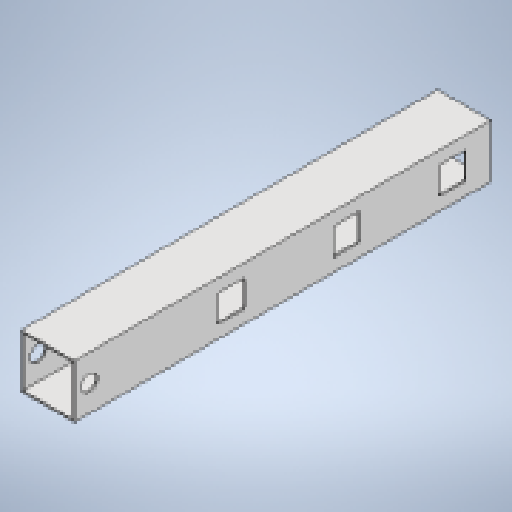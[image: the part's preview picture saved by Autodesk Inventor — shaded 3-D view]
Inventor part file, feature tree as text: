
AUTODESK INVENTOR PART (.ipt)
format: ipt  version: 2025.1 (Build 291241020, 241B)  size: 260,096 bytes
history: native  units: mm
features: sketch x4, projected_geometry x3, extrude x2, fillet x1
ambient origin geometry x8: Origin, YZ Plane, XZ Plane, XY Plane, X Axis, Y Axis, Z Axis, Center Point
bodies: Body1 (feature_tree)
feature tree (10):
  extrude  "Extrusion3"  Depth=60.0mm
  extrude  "Extrusion4"  Depth=2.0mm
  sketch  "Sketch11"  dims[d177=30.5mm]
  sketch  "Sketch13"  dims[d178=30.5mm d179=0.0mm d180=0.0mm d181=47.0mm d182=90.0mm d183=210.0mm d184=340.0mm d185=500.0mm d186=18.0mm d187=2.0mm]
  fillet  "Fillet1"  Radius=335.0mm
  sketch  "Sketch9"  dims[d61=500.0mm d172=60.0mm]
  sketch  "Sketch10"  dims[d173=60.0mm d174=2.0mm d175=335.0mm d176=0.0mm]
  projected_geometry  "Projected Loop3"
  projected_geometry  "Projected Loop4"
  projected_geometry  "Projected Loop5"
